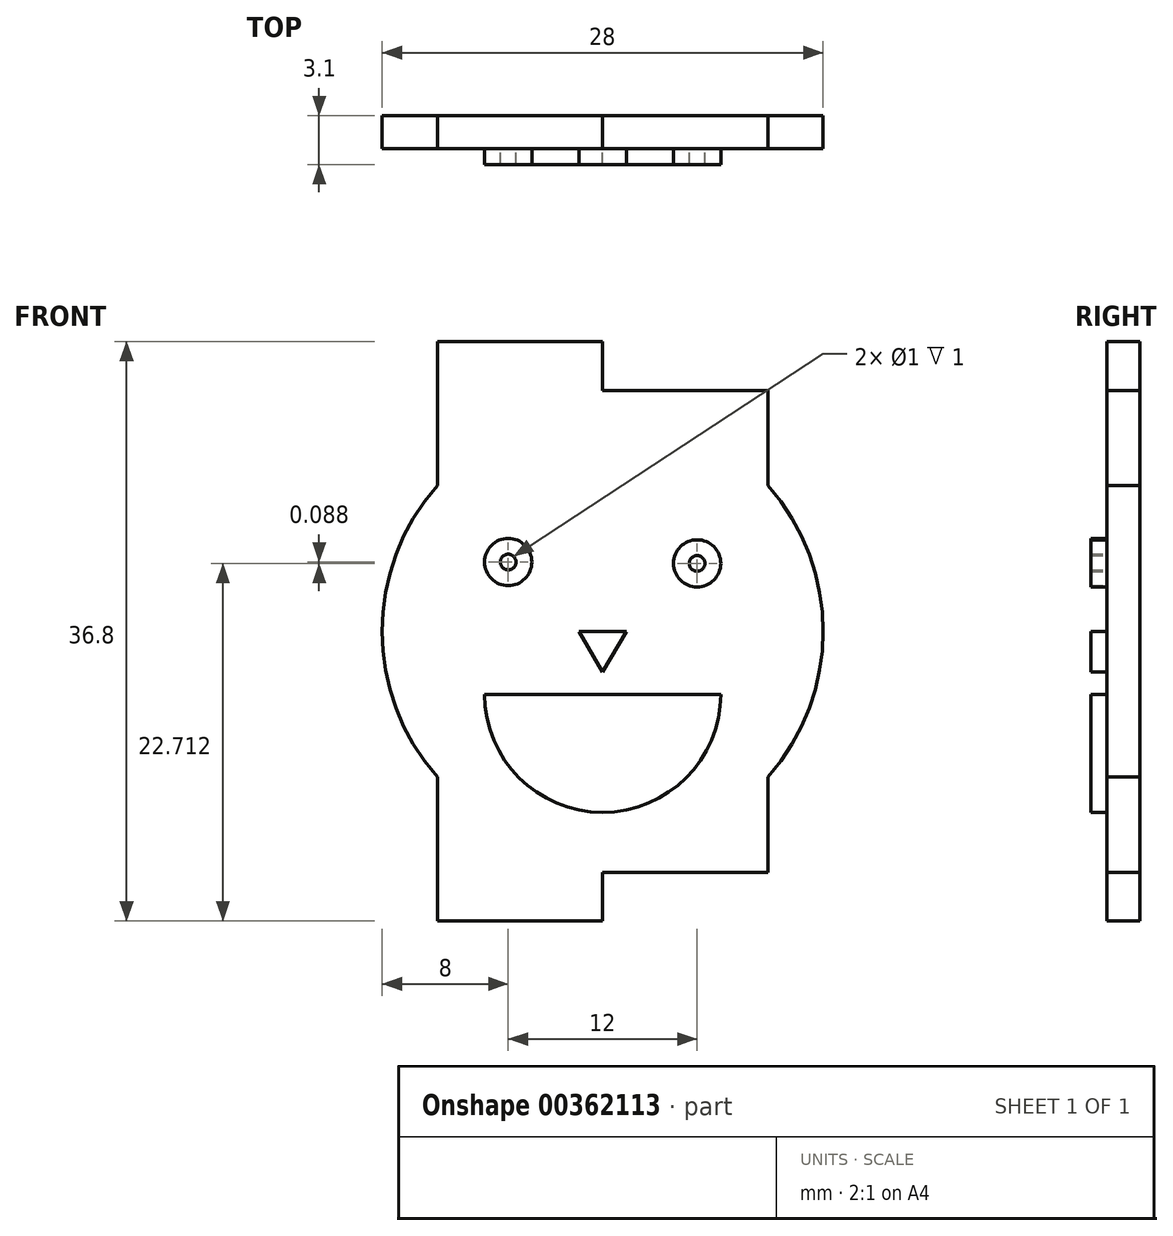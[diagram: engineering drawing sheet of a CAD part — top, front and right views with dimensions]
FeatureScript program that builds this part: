
annotation { "Feature Type Name" : "Feature", "Feature Type Description" : "" }
export const myFeature = defineFeature(function(context is Context, id is Id, definition is map)
    precondition{}
    {
        {
            var Q0;
            Q0=qCreatedBy(makeId("Front.planeOp"),FACE);
            var sketch = newSketch(context, id + "F0", { "sketchPlane" : qUnion([Q0])});
            skLineSegment(sketch, "E0", {"start": v(-10.5, -9.26) * mm, "end": v(-10.5, -18.4) * mm});
            skLineSegment(sketch, "E1", {"start": v(-10.5, -18.4) * mm, "end": v(0, -18.4) * mm});
            skLineSegment(sketch, "E2", {"start": v(0, -18.4) * mm, "end": v(0, -15.3) * mm});
            skLineSegment(sketch, "E3", {"start": v(0, -15.3) * mm, "end": v(10.5, -15.3) * mm});
            skLineSegment(sketch, "E4", {"start": v(-10.5, 9.26) * mm, "end": v(-10.5, 18.4) * mm});
            skLineSegment(sketch, "E5", {"start": v(-10.5, 18.4) * mm, "end": v(0, 18.4) * mm});
            skLineSegment(sketch, "E6", {"start": v(0, 18.4) * mm, "end": v(0, 15.3) * mm});
            skLineSegment(sketch, "E7", {"start": v(10.5, -15.3) * mm, "end": v(10.5, -9.26) * mm});
            skArc(sketch, "E8", {"start": v(-10.5, 9.26) * mm, "mid": v(-14, 0) * mm, "end": v(-10.5, -9.26) * mm});
            skLineSegment(sketch, "E9", {"start": v(0, 15.3) * mm, "end": v(10.5, 15.3) * mm});
            skLineSegment(sketch, "E10", {"start": v(10.5, 9.26) * mm, "end": v(10.5, 15.3) * mm});
            skPoint(sketch, "E11.orphan", {"position": v(-10.5, -9.26) * mm});
            skArc(sketch, "E12.trimOffspring", {"start": v(10.5, -9.26) * mm, "mid": v(14, 0) * mm, "end": v(10.5, 9.26) * mm});
            skSolve(sketch);
        }
        {
            var Q0;
            Q0=makeQuery(id+"F0.imprint","IMPRINT",FACE,{"disambiguationData":[TD([[makeQuery(id+"F0.imprint","IMPRINT",EDGE,{"derivedFrom":sQuery(id+"F0.wireOp",EDGE,"E0")}),1.0]])]});
            extrude(context, id + "F1", {"entities" : qUnion([Q0]), "oppositeDirection" : true, "depth" : 2.1 * mm});
        }
        {
            var Q0;
            Q0=qCreatedBy(makeId("Front.planeOp"),FACE);
            var sketch = newSketch(context, id + "F2", { "sketchPlane" : qUnion([Q0])});
            skCircle(sketch, "E13", {"center": v(-6, 4.4) * mm, "radius": 1.5 * mm});
            skCircle(sketch, "E14", {"center": v(-6, 4.4) * mm, "radius": 0.5 * mm});
            skCircle(sketch, "E15", {"center": v(6, 4.31) * mm, "radius": 1.5 * mm});
            skCircle(sketch, "E16", {"center": v(6, 4.31) * mm, "radius": 0.5 * mm});
            skSolve(sketch);
        }
        {
            var Q0;
            {var subQ0=sQuery(id+"F0.wireOp",EDGE,"E8");var subQ1=sQuery(id+"F0.wireOp",EDGE,"E7");var subQ2=sQuery(id+"F0.wireOp",EDGE,"E6");var subQ3=sQuery(id+"F0.wireOp",EDGE,"E5");var subQ4=sQuery(id+"F0.wireOp",EDGE,"E4");var subQ5=sQuery(id+"F0.wireOp",EDGE,"E9");var subQ6=sQuery(id+"F0.wireOp",EDGE,"E0");var subQ7=sQuery(id+"F0.wireOp",EDGE,"E3");var subQ8=sQuery(id+"F0.wireOp",EDGE,"E1");var subQ9=sQuery(id+"F0.wireOp",EDGE,"E2");var subQ10=sQuery(id+"F0.wireOp",EDGE,"E10");var subQ11=sQuery(id+"F0.wireOp",EDGE,"E12.trimOffspring");Q0=makeQuery(id+"FNFV11HQuz4OUgb_1.boolean.opBoolean","SPLIT",FACE,{"disambiguationData":[TD([makeQuery(id+"F1.opExtrude","SWEPT_FACE",FACE,{"disambiguationData":[OSD([subQ6])]})])],"derivedFrom":makeQuery(id+"F1.opExtrude","CAP_FACE",FACE,{"disambiguationData":[OSD([subQ6,subQ8,subQ9,subQ7,subQ4,subQ3,subQ2,subQ1,subQ0,subQ5,subQ10,subQ11])],"isStart":true})});}
            var sketch = newSketch(context, id + "F3", { "sketchPlane" : qUnion([Q0])});
            skLineSegment(sketch, "E17", {"start": v(-1.5, 0) * mm, "end": v(1.5, 0) * mm});
            skLineSegment(sketch, "E18", {"start": v(1.5, 0) * mm, "end": v(0, -2.6) * mm});
            skLineSegment(sketch, "E19", {"start": v(0, -2.6) * mm, "end": v(-1.5, 0) * mm});
            skSolve(sketch);
        }
        {
            var Q0;
            Q0=makeQuery(id+"F3.imprint","IMPRINT",FACE,{"disambiguationData":[TD([[makeQuery(id+"F3.imprint","IMPRINT",EDGE,{"derivedFrom":sQuery(id+"F3.wireOp",EDGE,"RzJObr4J-7PCg-ZiWl-yNxs-qPMMtmjhzAEr")}),-1.0]])]});
            var Q1;
            Q1=makeQuery(id+"F3.imprint","IMPRINT",FACE,{"disambiguationData":[TD([[makeQuery(id+"F3.imprint","IMPRINT",EDGE,{"derivedFrom":sQuery(id+"F3.wireOp",EDGE,"E17")}),-1.0]])]});
            extrude(context, id + "F4", {"entities" : qUnion([Q0, Q1]), "operationType" : NewBodyOperationType.ADD, "depth" : 1 * mm});
        }
        {
            var Q0;
            {var subQ0=sQuery(id+"F0.wireOp",EDGE,"E8");var subQ1=sQuery(id+"F0.wireOp",EDGE,"E7");var subQ2=sQuery(id+"F0.wireOp",EDGE,"E6");var subQ3=sQuery(id+"F0.wireOp",EDGE,"E5");var subQ4=sQuery(id+"F0.wireOp",EDGE,"E4");var subQ5=sQuery(id+"F0.wireOp",EDGE,"E9");var subQ6=sQuery(id+"F0.wireOp",EDGE,"E0");var subQ7=sQuery(id+"F0.wireOp",EDGE,"E3");var subQ8=sQuery(id+"F0.wireOp",EDGE,"E1");var subQ9=sQuery(id+"F0.wireOp",EDGE,"E2");var subQ10=sQuery(id+"F0.wireOp",EDGE,"E10");var subQ11=sQuery(id+"F0.wireOp",EDGE,"E12.trimOffspring");Q0=makeQuery(id+"FNFV11HQuz4OUgb_1.boolean.opBoolean","SPLIT",FACE,{"disambiguationData":[TD([makeQuery(id+"F1.opExtrude","SWEPT_FACE",FACE,{"disambiguationData":[OSD([subQ6])]})])],"derivedFrom":makeQuery(id+"F1.opExtrude","CAP_FACE",FACE,{"disambiguationData":[OSD([subQ6,subQ8,subQ9,subQ7,subQ4,subQ3,subQ2,subQ1,subQ0,subQ5,subQ10,subQ11])],"isStart":true})});}
            var sketch = newSketch(context, id + "F5", { "sketchPlane" : qUnion([Q0])});
            skArc(sketch, "E20", {"start": v(-7.5, -4) * mm, "mid": v(0, -11.5) * mm, "end": v(7.5, -4) * mm});
            skLineSegment(sketch, "E21", {"start": v(0, -4) * mm, "end": v(7.5, -4) * mm});
            skLineSegment(sketch, "E22", {"start": v(7.5, -4) * mm, "end": v(-7.5, -4) * mm});
            skSolve(sketch);
        }
        {
            var Q0;
            Q0=sQuery(id+"F5.wireOp",EDGE,"E22");
            var Q1;
            Q1=sQuery(id+"F5.wireOp",EDGE,"E20");
            extrude(context, id + "F6", {"bodyType" : ToolBodyType.SURFACE, "surfaceEntities" : qUnion([Q0, Q1]), "depth" : 1 * mm});
        }
        {
            var Q0;
            Q0=makeQuery(id+"F5.imprint","IMPRINT",FACE,{"disambiguationData":[TD([[makeQuery(id+"F5.imprint","IMPRINT",EDGE,{"derivedFrom":sQuery(id+"F5.wireOp",EDGE,"Q0vjRXVC-hn26-CX5H-HxAM-Eu5wQGO4rDhg.right")}),1.0]])]});
            var Q1;
            {var subQ0=sQuery(id+"F5.wireOp",EDGE,"E20");Q1=makeQuery(id+"F5.imprint","IMPRINT",FACE,{"disambiguationData":[TD([[makeQuery(id+"F5.imprint","IMPRINT",EDGE,{"derivedFrom":subQ0}),1.0]])]});}
            extrude(context, id + "F7", {"entities" : qUnion([Q0, Q1]), "operationType" : NewBodyOperationType.ADD, "depth" : 1 * mm});
        }
        {
            var Q0;
            Q0 = qSketchRegion(id + "F2", true);
            extrude(context, id + "F8", {"entities" : qUnion([Q0]), "operationType" : NewBodyOperationType.ADD, "depth" : 1 * mm});
        }
    });
